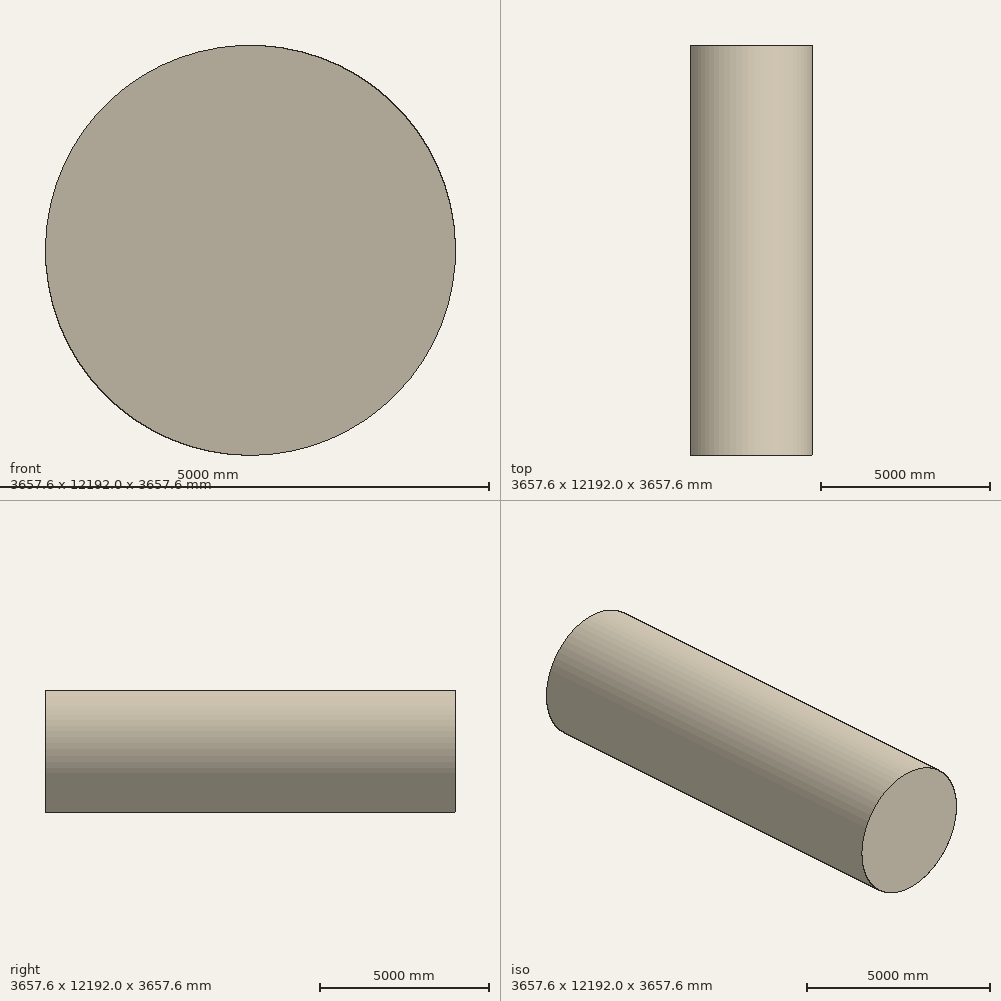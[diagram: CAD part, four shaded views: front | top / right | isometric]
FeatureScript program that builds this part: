
annotation { "Feature Type Name" : "Feature", "Feature Type Description" : "" }
export const myFeature = defineFeature(function(context is Context, id is Id, definition is map)
    precondition{}
    {
        {
            var Q0;
            Q0=qCreatedBy(makeId("Front.planeOp"),FACE);
            var sketch = newSketch(context, id + "F0", { "sketchPlane" : qUnion([Q0])});
            skCircle(sketch, "E0", {"center": v(0, 0) * mm, "radius": 1828.8 * mm});
            skSolve(sketch);
        }
        {
            var Q0;
            Q0=makeQuery(id+"F0.imprint","IMPRINT",FACE,{"disambiguationData":[TD([[makeQuery(id+"F0.imprint","IMPRINT",EDGE,{"derivedFrom":sQuery(id+"F0.wireOp",EDGE,"E0")}),1.0]])]});
            extrude(context, id + "F1", {"entities" : qUnion([Q0]), "depth" : 12192 * mm});
        }
    });
